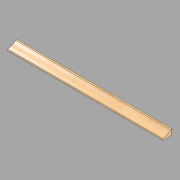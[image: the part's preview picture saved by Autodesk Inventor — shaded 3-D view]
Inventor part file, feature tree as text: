
AUTODESK INVENTOR PART (.ipt)
format: ipt  version: 2022.2 (Build 262287010, 287A)  size: 122,880 bytes
history: native  units: in
note: dims shown in document units (in); Inventor stores cm internally (conversion verified against a paired STEP export)
features: revolve x2, other x1, direct_edit x1
ambient origin geometry x8: Origin, YZ Plane, XZ Plane, XY Plane, X Axis, Y Axis, Z Axis, Center Point
bodies: Solid1 (feature_tree)
feature tree (4):
  other  "Jamb (Lower)"
  direct_edit  "Direct Edit2"
  revolve  "Rotate3"  [1 undecoded]
  revolve  "Rotate4"  [1 undecoded]
note: 2 required parameter values undecoded (feature->parameter linkage not recoverable at this tier; creation-order binding heuristic only, values carry confidence <= 0.55)
